# Revit family: Legrand coffret encastré métallique British standard
name_source: partatom
category: Equipement électrique
revit_build: Autodesk Revit 2018 (Build: 20170223_1515(x64)
units: mm (PartAtom-declared; Revit-internal decimal feet)

## family parameters
Basée sur le plan de construction = Non
Configuration du panneau = Deux colonnes, circuits au sein
Cote de connecteur circulaire = Utiliser le diamètre
Couper avec des vides une fois chargée = Non
Numéro OmniClass = 23.80.30.11.17
Partagée = Non
Point de calcul de pièce = Non
Titre OmniClass = Distribution Boards and Control Panels
Toujours verticalement = Oui
Type d'élément = Tableau de raccordement

## types (5) — shared parameters
Conditions Générale d'Utilisation = https://export.legrand.com
Couleur = Gris
Fabricant = Legrand
Hauteur = 236 mm
IP = IP 41
Matière = Métal
Modèle = Flush-mounting British standard
Puissance = 100A
URL = www.legrand.com
profondeur = 82 mm  [stored 0.269029 ft]

## per-type parameters (varying)
| type | 402505 | 402506 | 402507 | 402508 | 402509 | Bornier N | Bornier T | Largeur | nombre de modules |
| Coffret 402505 | Oui | Non | Non | Non | Non | 4 trous | 4 trous | 190 mm | 2+4 |
| Coffret 402506 | Non | Oui | Non | Non | Non | 6 trous | 6 trous | 230 mm  [stored 0.754593 ft] | 2+6 |
| Coffret 402507 | Non | Non | Oui | Non | Non | 8 trous | 8 trous | 260 mm  [stored 0.853018 ft] | 2+8 |
| Coffret 402508 | Non | Non | Non | Oui | Non | 12 trous | 12 trous | 336 mm  [stored 1.10236 ft] | 2+12 |
| Coffret 402509 | Non | Non | Non | Non | Oui | 16 trous | 16 trous | 408 mm | 2+14 |

note: [stored X ft] marks values corroborated as IEEE doubles in the binary element streams (Revit-internal decimal feet)
